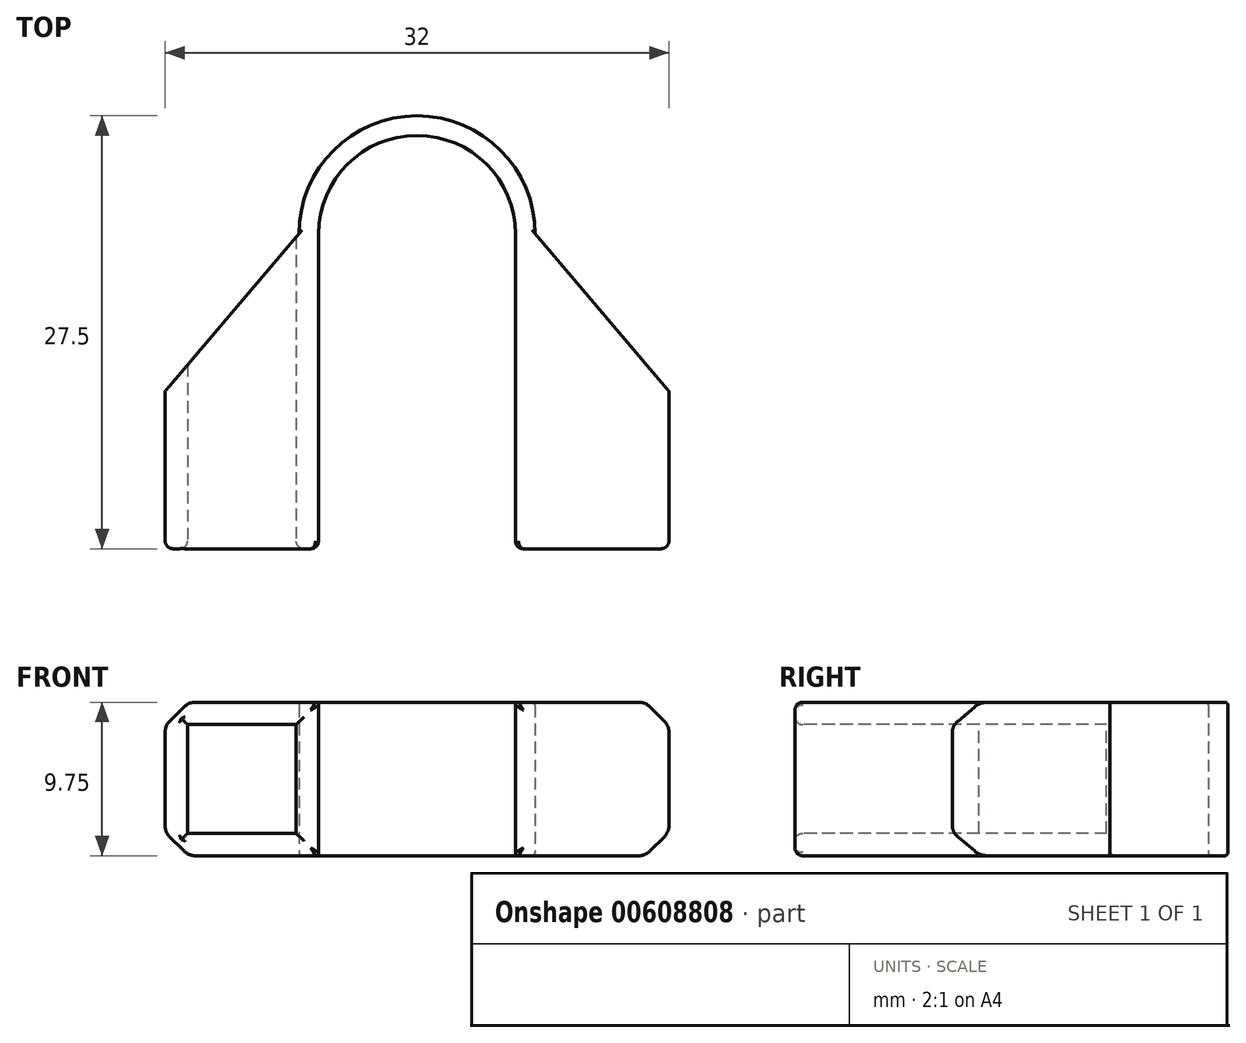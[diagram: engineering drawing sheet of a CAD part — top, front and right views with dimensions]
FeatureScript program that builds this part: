
annotation { "Feature Type Name" : "Feature", "Feature Type Description" : "" }
export const myFeature = defineFeature(function(context is Context, id is Id, definition is map)
    precondition{}
    {
        {
            var Q0;
            Q0=qCreatedBy(makeId("Top.planeOp"),FACE);
            var sketch = newSketch(context, id + "F0", { "sketchPlane" : qUnion([Q0])});
            skArc(sketch, "E0", {"start": v(7.5, 0) * mm, "mid": v(0, 7.5) * mm, "end": v(-7.5, 0) * mm});
            skArc(sketch, "E1", {"start": v(6.25, 0) * mm, "mid": v(0, 6.25) * mm, "end": v(-6.25, 0) * mm});
            skLineSegment(sketch, "E2", {"start": v(-6.25, 0) * mm, "end": v(-6.25, -20) * mm});
            skLineSegment(sketch, "E3", {"start": v(-6.25, -20) * mm, "end": v(-16, -20) * mm});
            skLineSegment(sketch, "E4", {"start": v(-16, -20) * mm, "end": v(-16, -10) * mm});
            skLineSegment(sketch, "E5", {"start": v(-16, -10) * mm, "end": v(-7.5, 0) * mm});
            skLineSegment(sketch, "E6.MirrorCS", {"start": v(6.25, 0) * mm, "end": v(6.25, -20) * mm});
            skLineSegment(sketch, "E7.MirrorCS", {"start": v(16, -10) * mm, "end": v(7.5, 0) * mm});
            skLineSegment(sketch, "E8.MirrorCS", {"start": v(16, -20) * mm, "end": v(16, -10) * mm});
            skLineSegment(sketch, "E9.MirrorCS", {"start": v(6.25, -20) * mm, "end": v(16, -20) * mm});
            skSolve(sketch);
        }
        {
            var Q0;
            Q0 = qSketchRegion(id + "F0", true);
            extrude(context, id + "F1", {"entities" : qUnion([Q0]), "depth" : 9.75 * mm, "offsetDistance" : 25 * mm});
        }
        {
            var Q0;
            Q0=makeQuery(id+"F1.opExtrude","SWEPT_FACE",FACE,{"disambiguationData":[OSD([sQuery(id+"F0.wireOp",EDGE,"E3")])]});
            var sketch = newSketch(context, id + "F2", { "sketchPlane" : qUnion([Q0])});
            skLineSegment(sketch, "E10.bottom", {"start": v(-14.57, 8.33) * mm, "end": v(-7.67, 8.33) * mm});
            skLineSegment(sketch, "E10.top", {"start": v(-14.57, 1.43) * mm, "end": v(-7.67, 1.43) * mm});
            skLineSegment(sketch, "E10.left", {"start": v(-14.57, 8.33) * mm, "end": v(-14.57, 1.43) * mm});
            skLineSegment(sketch, "E10.right", {"start": v(-7.67, 8.33) * mm, "end": v(-7.67, 1.43) * mm});
            skSolve(sketch);
        }
        {
            var Q0;
            Q0 = qSketchRegion(id + "F2", true);
            extrude(context, id + "F3", {"entities" : qUnion([Q0]), "operationType" : NewBodyOperationType.REMOVE, "oppositeDirection" : true, "depth" : 25 * mm, "offsetDistance" : 25 * mm});
        }
        {
            var Q0;
            Q0=makeQuery(id+"F1.opExtrude","CAP_EDGE",EDGE,{"disambiguationData":[OSD([sQuery(id+"F0.wireOp",EDGE,"E4")])],"isStart":true});
            var Q1;
            Q1=makeQuery(id+"F1.opExtrude","CAP_EDGE",EDGE,{"disambiguationData":[OSD([sQuery(id+"F0.wireOp",EDGE,"E4")])],"isStart":false});
            var Q2;
            Q2=makeQuery(id+"F1.opExtrude","CAP_EDGE",EDGE,{"disambiguationData":[OSD([sQuery(id+"F0.wireOp",EDGE,"E8.MirrorCS")])],"isStart":false});
            var Q3;
            Q3=makeQuery(id+"F1.opExtrude","CAP_EDGE",EDGE,{"disambiguationData":[OSD([sQuery(id+"F0.wireOp",EDGE,"E8.MirrorCS")])],"isStart":true});
            chamfer(context, id + "F4", {"entities" : qUnion([Q0, Q1, Q2, Q3]), "width" : 1.5 * mm, "tangentPropagation" : true});
        }
        {
            var Q0;
            {var subQ0=sQuery(id+"F0.wireOp",EDGE,"E4");Q0=makeQuery(id+"F4.opChamfer","BLEND_EDGE",EDGE,{"blendedFrom":[makeQuery(id+"F1.opExtrude","CAP_EDGE",EDGE,{"disambiguationData":[OSD([subQ0])],"isStart":true}),makeQuery(id+"F1.opExtrude","CAP_FACE",FACE,{"disambiguationData":[OSD([sQuery(id+"F0.wireOp",EDGE,"E0"),sQuery(id+"F0.wireOp",EDGE,"E1"),sQuery(id+"F0.wireOp",EDGE,"E2"),sQuery(id+"F0.wireOp",EDGE,"E3"),subQ0,sQuery(id+"F0.wireOp",EDGE,"E5"),sQuery(id+"F0.wireOp",EDGE,"E6.MirrorCS"),sQuery(id+"F0.wireOp",EDGE,"E7.MirrorCS"),sQuery(id+"F0.wireOp",EDGE,"E8.MirrorCS"),sQuery(id+"F0.wireOp",EDGE,"E9.MirrorCS")])],"isStart":true})],"blendedInto":[makeQuery(id+"F1.opExtrude","CAP_FACE",FACE,{"disambiguationData":[OSD([sQuery(id+"F0.wireOp",EDGE,"E0"),sQuery(id+"F0.wireOp",EDGE,"E1"),sQuery(id+"F0.wireOp",EDGE,"E2"),sQuery(id+"F0.wireOp",EDGE,"E3"),subQ0,sQuery(id+"F0.wireOp",EDGE,"E5"),sQuery(id+"F0.wireOp",EDGE,"E6.MirrorCS"),sQuery(id+"F0.wireOp",EDGE,"E7.MirrorCS"),sQuery(id+"F0.wireOp",EDGE,"E8.MirrorCS"),sQuery(id+"F0.wireOp",EDGE,"E9.MirrorCS")])],"isStart":true})]});}
            var Q1;
            {var subQ0=sQuery(id+"F0.wireOp",EDGE,"E4");Q1=makeQuery(id+"F4.opChamfer","BLEND_EDGE",EDGE,{"blendedFrom":[makeQuery(id+"F1.opExtrude","CAP_EDGE",EDGE,{"disambiguationData":[OSD([subQ0])],"isStart":true}),makeQuery(id+"F1.opExtrude","SWEPT_FACE",FACE,{"disambiguationData":[OSD([subQ0])]})],"blendedInto":[makeQuery(id+"F1.opExtrude","SWEPT_FACE",FACE,{"disambiguationData":[OSD([subQ0])]})]});}
            var Q2;
            {var subQ0=sQuery(id+"F0.wireOp",EDGE,"E4");Q2=makeQuery(id+"F4.opChamfer","BLEND_EDGE",EDGE,{"blendedFrom":[makeQuery(id+"F1.opExtrude","CAP_EDGE",EDGE,{"disambiguationData":[OSD([subQ0])],"isStart":false}),makeQuery(id+"F1.opExtrude","SWEPT_FACE",FACE,{"disambiguationData":[OSD([subQ0])]})],"blendedInto":[makeQuery(id+"F1.opExtrude","SWEPT_FACE",FACE,{"disambiguationData":[OSD([subQ0])]})]});}
            var Q3;
            {var subQ0=sQuery(id+"F0.wireOp",EDGE,"E4");Q3=makeQuery(id+"F4.opChamfer","BLEND_EDGE",EDGE,{"blendedFrom":[makeQuery(id+"F1.opExtrude","CAP_EDGE",EDGE,{"disambiguationData":[OSD([subQ0])],"isStart":false}),makeQuery(id+"F1.opExtrude","CAP_FACE",FACE,{"disambiguationData":[OSD([sQuery(id+"F0.wireOp",EDGE,"E0"),sQuery(id+"F0.wireOp",EDGE,"E1"),sQuery(id+"F0.wireOp",EDGE,"E2"),sQuery(id+"F0.wireOp",EDGE,"E3"),subQ0,sQuery(id+"F0.wireOp",EDGE,"E5"),sQuery(id+"F0.wireOp",EDGE,"E6.MirrorCS"),sQuery(id+"F0.wireOp",EDGE,"E7.MirrorCS"),sQuery(id+"F0.wireOp",EDGE,"E8.MirrorCS"),sQuery(id+"F0.wireOp",EDGE,"E9.MirrorCS")])],"isStart":false})],"blendedInto":[makeQuery(id+"F1.opExtrude","CAP_FACE",FACE,{"disambiguationData":[OSD([sQuery(id+"F0.wireOp",EDGE,"E0"),sQuery(id+"F0.wireOp",EDGE,"E1"),sQuery(id+"F0.wireOp",EDGE,"E2"),sQuery(id+"F0.wireOp",EDGE,"E3"),subQ0,sQuery(id+"F0.wireOp",EDGE,"E5"),sQuery(id+"F0.wireOp",EDGE,"E6.MirrorCS"),sQuery(id+"F0.wireOp",EDGE,"E7.MirrorCS"),sQuery(id+"F0.wireOp",EDGE,"E8.MirrorCS"),sQuery(id+"F0.wireOp",EDGE,"E9.MirrorCS")])],"isStart":false})]});}
            var Q4;
            {var subQ0=sQuery(id+"F0.wireOp",EDGE,"E8.MirrorCS");Q4=makeQuery(id+"F4.opChamfer","BLEND_EDGE",EDGE,{"blendedFrom":[makeQuery(id+"F1.opExtrude","CAP_EDGE",EDGE,{"disambiguationData":[OSD([subQ0])],"isStart":false}),makeQuery(id+"F1.opExtrude","CAP_FACE",FACE,{"disambiguationData":[OSD([sQuery(id+"F0.wireOp",EDGE,"E0"),sQuery(id+"F0.wireOp",EDGE,"E1"),sQuery(id+"F0.wireOp",EDGE,"E2"),sQuery(id+"F0.wireOp",EDGE,"E3"),sQuery(id+"F0.wireOp",EDGE,"E4"),sQuery(id+"F0.wireOp",EDGE,"E5"),sQuery(id+"F0.wireOp",EDGE,"E6.MirrorCS"),sQuery(id+"F0.wireOp",EDGE,"E7.MirrorCS"),subQ0,sQuery(id+"F0.wireOp",EDGE,"E9.MirrorCS")])],"isStart":false})],"blendedInto":[makeQuery(id+"F1.opExtrude","CAP_FACE",FACE,{"disambiguationData":[OSD([sQuery(id+"F0.wireOp",EDGE,"E0"),sQuery(id+"F0.wireOp",EDGE,"E1"),sQuery(id+"F0.wireOp",EDGE,"E2"),sQuery(id+"F0.wireOp",EDGE,"E3"),sQuery(id+"F0.wireOp",EDGE,"E4"),sQuery(id+"F0.wireOp",EDGE,"E5"),sQuery(id+"F0.wireOp",EDGE,"E6.MirrorCS"),sQuery(id+"F0.wireOp",EDGE,"E7.MirrorCS"),subQ0,sQuery(id+"F0.wireOp",EDGE,"E9.MirrorCS")])],"isStart":false})]});}
            var Q5;
            {var subQ0=sQuery(id+"F0.wireOp",EDGE,"E8.MirrorCS");Q5=makeQuery(id+"F4.opChamfer","BLEND_EDGE",EDGE,{"blendedFrom":[makeQuery(id+"F1.opExtrude","CAP_EDGE",EDGE,{"disambiguationData":[OSD([subQ0])],"isStart":false}),makeQuery(id+"F1.opExtrude","SWEPT_FACE",FACE,{"disambiguationData":[OSD([subQ0])]})],"blendedInto":[makeQuery(id+"F1.opExtrude","SWEPT_FACE",FACE,{"disambiguationData":[OSD([subQ0])]})]});}
            var Q6;
            {var subQ0=sQuery(id+"F0.wireOp",EDGE,"E8.MirrorCS");Q6=makeQuery(id+"F4.opChamfer","BLEND_EDGE",EDGE,{"blendedFrom":[makeQuery(id+"F1.opExtrude","CAP_EDGE",EDGE,{"disambiguationData":[OSD([subQ0])],"isStart":true}),makeQuery(id+"F1.opExtrude","SWEPT_FACE",FACE,{"disambiguationData":[OSD([subQ0])]})],"blendedInto":[makeQuery(id+"F1.opExtrude","SWEPT_FACE",FACE,{"disambiguationData":[OSD([subQ0])]})]});}
            var Q7;
            {var subQ0=sQuery(id+"F0.wireOp",EDGE,"E8.MirrorCS");Q7=makeQuery(id+"F4.opChamfer","BLEND_EDGE",EDGE,{"blendedFrom":[makeQuery(id+"F1.opExtrude","CAP_EDGE",EDGE,{"disambiguationData":[OSD([subQ0])],"isStart":true}),makeQuery(id+"F1.opExtrude","CAP_FACE",FACE,{"disambiguationData":[OSD([sQuery(id+"F0.wireOp",EDGE,"E0"),sQuery(id+"F0.wireOp",EDGE,"E1"),sQuery(id+"F0.wireOp",EDGE,"E2"),sQuery(id+"F0.wireOp",EDGE,"E3"),sQuery(id+"F0.wireOp",EDGE,"E4"),sQuery(id+"F0.wireOp",EDGE,"E5"),sQuery(id+"F0.wireOp",EDGE,"E6.MirrorCS"),sQuery(id+"F0.wireOp",EDGE,"E7.MirrorCS"),subQ0,sQuery(id+"F0.wireOp",EDGE,"E9.MirrorCS")])],"isStart":true})],"blendedInto":[makeQuery(id+"F1.opExtrude","CAP_FACE",FACE,{"disambiguationData":[OSD([sQuery(id+"F0.wireOp",EDGE,"E0"),sQuery(id+"F0.wireOp",EDGE,"E1"),sQuery(id+"F0.wireOp",EDGE,"E2"),sQuery(id+"F0.wireOp",EDGE,"E3"),sQuery(id+"F0.wireOp",EDGE,"E4"),sQuery(id+"F0.wireOp",EDGE,"E5"),sQuery(id+"F0.wireOp",EDGE,"E6.MirrorCS"),sQuery(id+"F0.wireOp",EDGE,"E7.MirrorCS"),subQ0,sQuery(id+"F0.wireOp",EDGE,"E9.MirrorCS")])],"isStart":true})]});}
            fillet(context, id + "F5", {"entities" : qUnion([Q0, Q1, Q2, Q3, Q4, Q5, Q6, Q7]), "radius" : 1 * mm, "tangentPropagation" : true, "allowEdgeOverflow" : false});
        }
        {
            var Q0;
            Q0=makeQuery(id+"F1.opExtrude","SWEPT_FACE",FACE,{"disambiguationData":[OSD([sQuery(id+"F0.wireOp",EDGE,"E3")])]});
            var Q1;
            Q1=makeQuery(id+"F1.opExtrude","SWEPT_FACE",FACE,{"disambiguationData":[OSD([sQuery(id+"F0.wireOp",EDGE,"E9.MirrorCS")])]});
            fillet(context, id + "F6", {"entities" : qUnion([Q0, Q1]), "radius" : .5 * mm, "tangentPropagation" : true, "allowEdgeOverflow" : false});
        }
        {
            var Q0;
            Q0=makeQuery(id+"F1.opExtrude","CAP_EDGE",EDGE,{"disambiguationData":[OSD([sQuery(id+"F0.wireOp",EDGE,"E2")])],"isStart":false});
            var Q1;
            Q1=makeQuery(id+"F1.opExtrude","CAP_EDGE",EDGE,{"disambiguationData":[OSD([sQuery(id+"F0.wireOp",EDGE,"E2")])],"isStart":true});
            var Q2;
            Q2=makeQuery(id+"F1.opExtrude","CAP_EDGE",EDGE,{"disambiguationData":[OSD([sQuery(id+"F0.wireOp",EDGE,"E0")])],"isStart":true});
            var Q3;
            Q3=makeQuery(id+"F1.opExtrude","CAP_EDGE",EDGE,{"disambiguationData":[OSD([sQuery(id+"F0.wireOp",EDGE,"E0")])],"isStart":false});
            fillet(context, id + "F7", {"entities" : qUnion([Q0, Q1, Q2, Q3]), "radius" : .2 * mm, "tangentPropagation" : true, "allowEdgeOverflow" : false});
        }
    });
